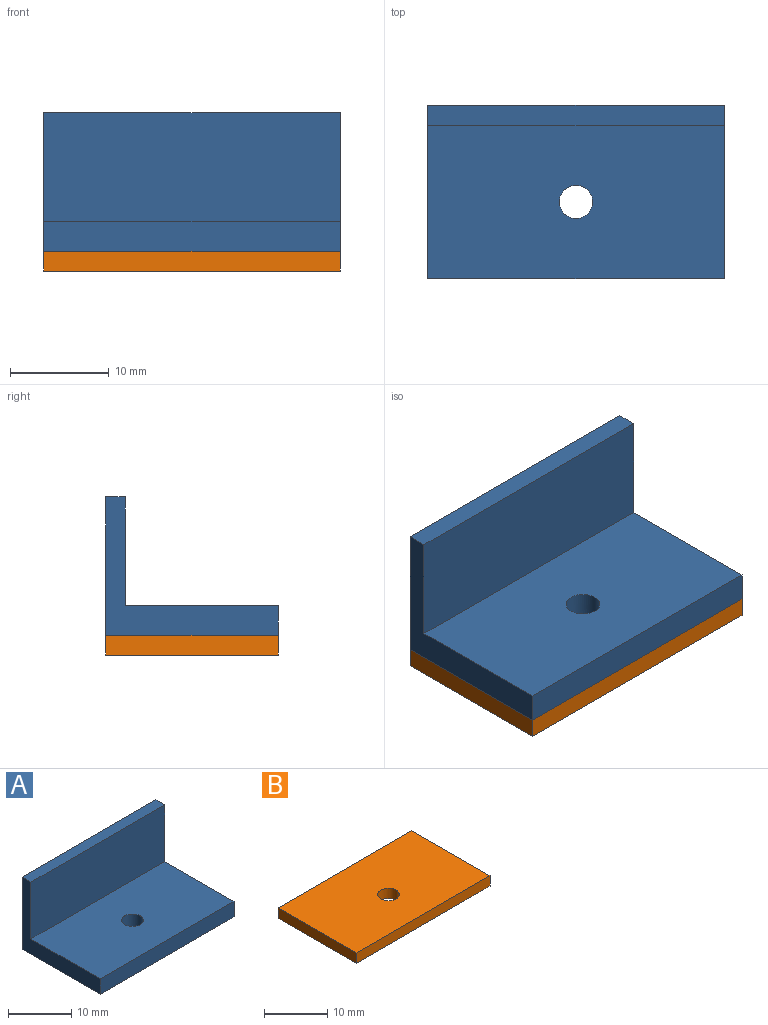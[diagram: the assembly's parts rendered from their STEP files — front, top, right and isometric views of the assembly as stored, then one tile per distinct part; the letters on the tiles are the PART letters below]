
ASSEMBLY  parts=2 mates=1
PART A: 9 faces, bbox 30x17.5x14 mm
  f0: plane 30x11mm, normal (0,-1,0), area 330mm2, adj f1,f2,f4,f6
  f1: plane 30x2mm, normal (0,0,1), area 60mm2, adj f0,f2,f4,f5
  f2: plane 17.5x14mm, normal (-1,0,0), area 74.5mm2, adj f0,f1,f3,f5,f6,f7
  f3: plane 30x17.5mm, normal (0,0,-1), area 515.9mm2, adj f2,f4,f5,f7,f8
  f4: plane 17.5x14mm, normal (1,0,0), area 74.5mm2, adj f0,f1,f3,f5,f6,f7
  f5: plane 30x14mm, normal (0,1,0), area 420mm2, adj f1,f2,f3,f4
  f6: plane 30x15.5mm, normal (0,0,1), area 455.9mm2, adj f0,f2,f4,f7,f8
  f7: plane 30x3mm, normal (0,-1,0), area 90mm2, adj f2,f3,f4,f6
  f8: cylinder r=1.7mm len=3.4mm, axis (0,0,-1), area 32mm2, adj f3,f6
PART B: 7 faces, bbox 30x17.5x2 mm
  f0: plane 30x17.5mm, normal (0,0,1), area 515.9mm2, adj f1,f3,f4,f5,f6
  f1: plane 17.5x2mm, normal (-1,0,0), area 35mm2, adj f0,f2,f4,f5
  f2: plane 30x17.5mm, normal (0,0,-1), area 515.9mm2, adj f1,f3,f4,f5,f6
  f3: plane 17.5x2mm, normal (1,0,0), area 35mm2, adj f0,f2,f4,f5
  f4: plane 30x2mm, normal (0,1,0), area 60mm2, adj f0,f1,f2,f3
  f5: plane 30x2mm, normal (0,-1,0), area 60mm2, adj f0,f1,f2,f3
  f6: cylinder r=1.7mm len=3.4mm, axis (0,0,-1), area 21.4mm2, adj f0,f2
PLACE A t=(-7.75,1.24,-1.56)mm
PLACE B t=(-7.75,1.24,-9.56)mm
MATE parallel B.f0 <-> A.f3  axis (0,0,1) through (-7.75,-5.5,-8.56)mm
